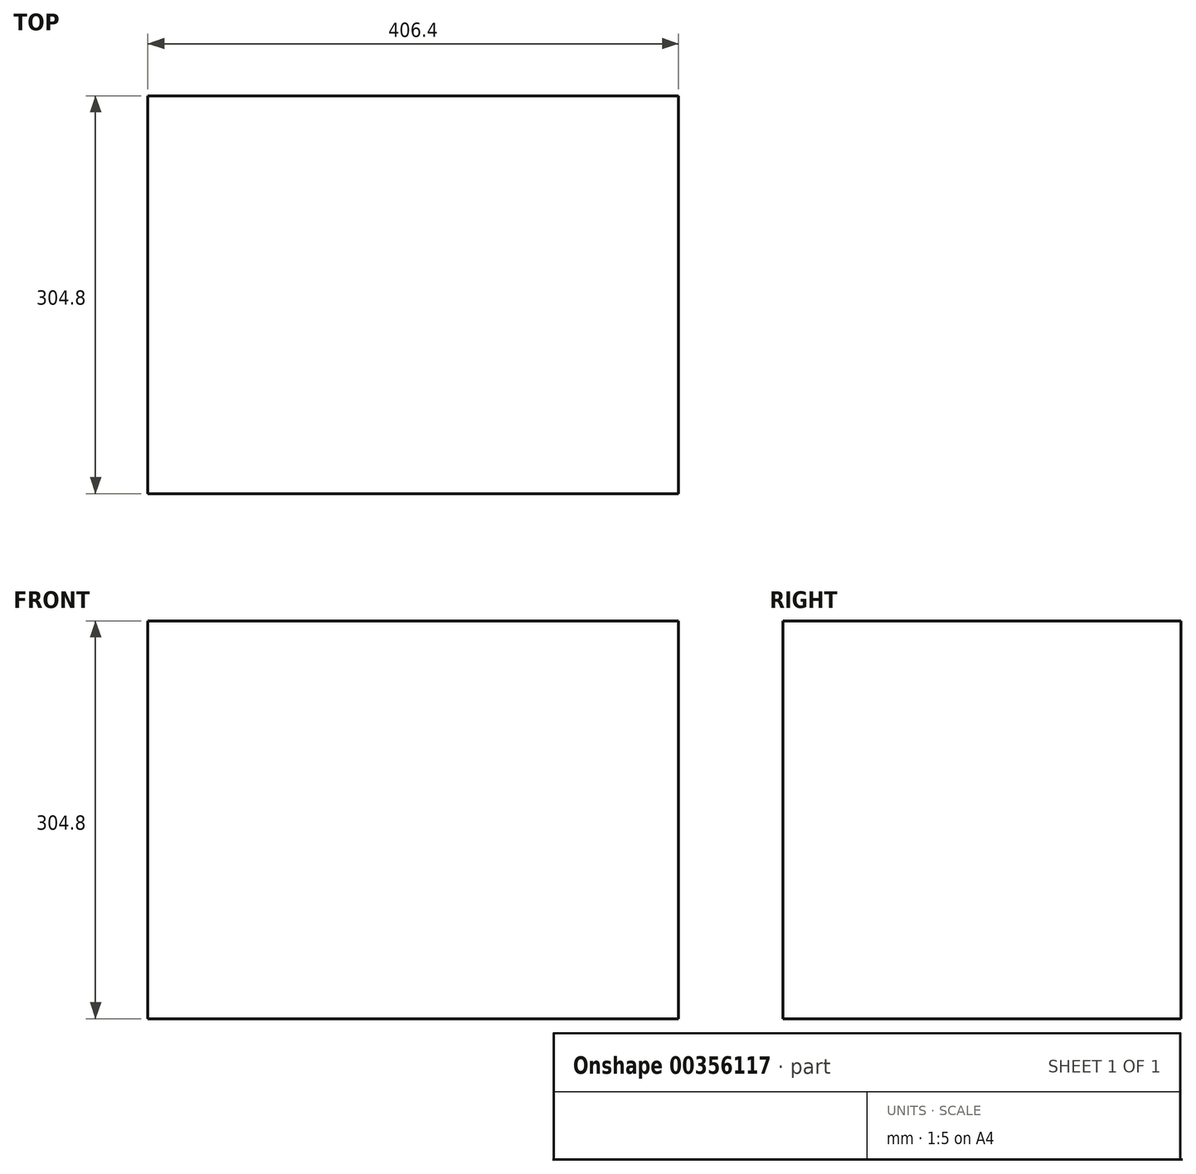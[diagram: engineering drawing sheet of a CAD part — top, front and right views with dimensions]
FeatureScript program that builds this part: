
annotation { "Feature Type Name" : "Feature", "Feature Type Description" : "" }
export const myFeature = defineFeature(function(context is Context, id is Id, definition is map)
    precondition{}
    {
        {
            var Q0;
            Q0=qCreatedBy(makeId("Top.planeOp"),FACE);
            var sketch = newSketch(context, id + "F0", { "sketchPlane" : qUnion([Q0])});
            skLineSegment(sketch, "E0.bottom", {"start": v(-203.2, 152.4) * mm, "end": v(203.2, 152.4) * mm});
            skLineSegment(sketch, "E0.top", {"start": v(-203.2, -152.4) * mm, "end": v(203.2, -152.4) * mm});
            skLineSegment(sketch, "E0.left", {"start": v(-203.2, 152.4) * mm, "end": v(-203.2, -152.4) * mm});
            skLineSegment(sketch, "E0.right", {"start": v(203.2, 152.4) * mm, "end": v(203.2, -152.4) * mm});
            skPoint(sketch, "E0.middle", {"position": v(0, 0) * mm});
            skSolve(sketch);
        }
        {
            var Q0;
            Q0=makeQuery(id+"F0.imprint","IMPRINT",FACE,{"disambiguationData":[TD([[makeQuery(id+"F0.imprint","IMPRINT",EDGE,{"derivedFrom":sQuery(id+"F0.wireOp",EDGE,"E0.bottom")}),-1.0]])]});
            extrude(context, id + "F1", {"entities" : qUnion([Q0]), "depth" : 304.8 * mm, "offsetDistance" : 25.4 * mm});
        }
    });
